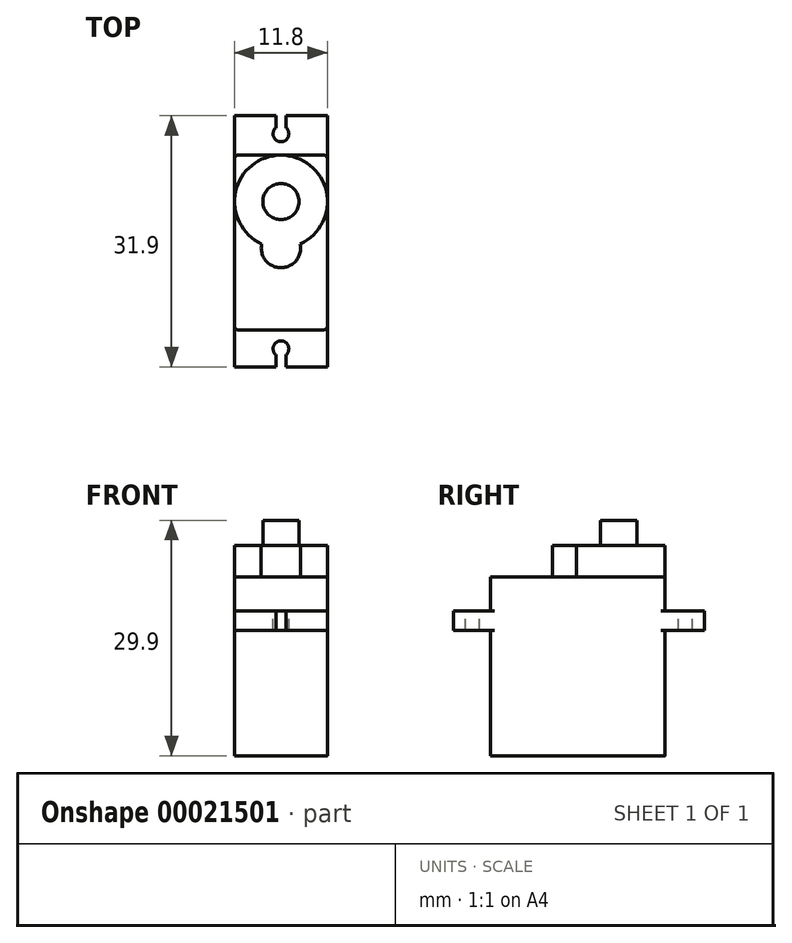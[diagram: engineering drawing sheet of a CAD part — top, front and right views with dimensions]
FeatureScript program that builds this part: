
annotation { "Feature Type Name" : "Feature", "Feature Type Description" : "" }
export const myFeature = defineFeature(function(context is Context, id is Id, definition is map)
    precondition{}
    {
        {
            var Q0;
            Q0=qCreatedBy(makeId("Top.planeOp"),FACE);
            var sketch = newSketch(context, id + "F0", { "sketchPlane" : qUnion([Q0])});
            skLineSegment(sketch, "E0", {"start": v(0, 0.5) * mm, "end": v(0, 21.7) * mm});
            skLineSegment(sketch, "E1", {"start": v(0.5, 22.2) * mm, "end": v(11.3, 22.2) * mm});
            skLineSegment(sketch, "E2", {"start": v(11.8, 21.7) * mm, "end": v(11.8, 0.5) * mm});
            skLineSegment(sketch, "E3", {"start": v(11.3, 0) * mm, "end": v(0.5, 0) * mm});
            skPoint(sketch, "E4.visualSharp", {"position": v(0, 22.2) * mm});
            skArc(sketch, "E4.filletArc", {"start": v(0.5, 22.2) * mm, "mid": v(0.15, 22.05) * mm, "end": v(0, 21.7) * mm});
            skPoint(sketch, "E5.visualSharp", {"position": v(11.8, 22.2) * mm});
            skArc(sketch, "E5.filletArc", {"start": v(11.8, 21.7) * mm, "mid": v(11.65, 22.05) * mm, "end": v(11.3, 22.2) * mm});
            skPoint(sketch, "E6.visualSharp", {"position": v(11.8, 0) * mm});
            skArc(sketch, "E6.filletArc", {"start": v(11.3, 0) * mm, "mid": v(11.65, 0.15) * mm, "end": v(11.8, 0.5) * mm});
            skPoint(sketch, "E7.visualSharp", {"position": v(0, 0) * mm});
            skArc(sketch, "E7.filletArc", {"start": v(0, 0.5) * mm, "mid": v(0.15, 0.15) * mm, "end": v(0.5, 0) * mm});
            skSolve(sketch);
        }
        {
            var Q0;
            Q0=makeQuery(id+"F0.imprint","IMPRINT",FACE,{"disambiguationData":[TD([[makeQuery(id+"F0.imprint","IMPRINT",EDGE,{"derivedFrom":sQuery(id+"F0.wireOp",EDGE,"E0")}),-1.0]])]});
            extrude(context, id + "F1", {"entities" : qUnion([Q0]), "depth" : 16 * mm});
        }
        {
            var Q0;
            Q0=makeQuery(id+"F1.opExtrude","CAP_FACE",FACE,{"disambiguationData":[OSD([sQuery(id+"F0.wireOp",EDGE,"E0"),sQuery(id+"F0.wireOp",EDGE,"E1"),sQuery(id+"F0.wireOp",EDGE,"E2"),sQuery(id+"F0.wireOp",EDGE,"E3"),sQuery(id+"F0.wireOp",EDGE,"E4.filletArc"),sQuery(id+"F0.wireOp",EDGE,"E5.filletArc"),sQuery(id+"F0.wireOp",EDGE,"E6.filletArc"),sQuery(id+"F0.wireOp",EDGE,"E7.filletArc")])],"isStart":false});
            extrude(context, id + "F2", {"entities" : qUnion([Q0]), "operationType" : NewBodyOperationType.ADD, "depth" : 6.7 * mm});
        }
        {
            var Q0;
            Q0=makeQuery(id+"F2.opExtrude","CAP_FACE",FACE,{"disambiguationData":[OSD([sQuery(id+"F0.wireOp",EDGE,"E0"),sQuery(id+"F0.wireOp",EDGE,"E1"),sQuery(id+"F0.wireOp",EDGE,"E2"),sQuery(id+"F0.wireOp",EDGE,"E3"),sQuery(id+"F0.wireOp",EDGE,"E4.filletArc"),sQuery(id+"F0.wireOp",EDGE,"E5.filletArc"),sQuery(id+"F0.wireOp",EDGE,"E6.filletArc"),sQuery(id+"F0.wireOp",EDGE,"E7.filletArc")])],"isStart":false});
            var sketch = newSketch(context, id + "F3", { "sketchPlane" : qUnion([Q0])});
            skLineSegment(sketch, "E8", {"start": v(0, 16.3) * mm, "end": v(11.8, 16.3) * mm, "construction": true});
            skArc(sketch, "E9", {"start": v(8.34, 10.93) * mm, "mid": v(5.9, 22.2) * mm, "end": v(3.46, 10.93) * mm});
            skLineSegment(sketch, "E10", {"start": v(5.9, 16.3) * mm, "end": v(5.9, 5.27) * mm, "construction": true});
            skArc(sketch, "E11", {"start": v(3.46, 10.93) * mm, "mid": v(5.9, 7.9) * mm, "end": v(8.34, 10.93) * mm});
            skSolve(sketch);
        }
        {
            var Q0;
            {var subQ0=sQuery(id+"F3.wireOp",EDGE,"E11");Q0=makeQuery(id+"F3.imprint","IMPRINT",FACE,{"disambiguationData":[TD([[makeQuery(id+"F3.imprint","IMPRINT",EDGE,{"derivedFrom":subQ0}),1.0]])]});}
            extrude(context, id + "F4", {"entities" : qUnion([Q0]), "operationType" : NewBodyOperationType.ADD, "depth" : 4 * mm});
        }
        {
            var Q0;
            Q0=makeQuery(id+"F4.opExtrude","CAP_FACE",FACE,{"disambiguationData":[OSD([sQuery(id+"F3.wireOp",EDGE,"E9"),sQuery(id+"F3.wireOp",EDGE,"E11")])],"isStart":false});
            var sketch = newSketch(context, id + "F5", { "sketchPlane" : qUnion([Q0])});
            skLineSegment(sketch, "E12", {"start": v(5.9, 22.2) * mm, "end": v(5.9, 7.9) * mm, "construction": true});
            skLineSegment(sketch, "E13", {"start": v(0, 16.3) * mm, "end": v(11.8, 16.3) * mm, "construction": true});
            skCircle(sketch, "E14", {"center": v(5.9, 16.3) * mm, "radius": 2.3 * mm});
            skSolve(sketch);
        }
        {
            var Q0;
            Q0=makeQuery(id+"F5.imprint","IMPRINT",FACE,{"disambiguationData":[TD([[makeQuery(id+"F5.imprint","IMPRINT",EDGE,{"derivedFrom":sQuery(id+"F5.wireOp",EDGE,"E14")}),1.0]])]});
            extrude(context, id + "F6", {"entities" : qUnion([Q0]), "operationType" : NewBodyOperationType.ADD, "depth" : 3.2 * mm});
        }
        {
            var Q0;
            {var subQ0=sQuery(id+"F0.wireOp",EDGE,"E3");Q0=makeQuery(id+"F2.boolean.opBoolean","MERGE",FACE,{"derivedFrom":[makeQuery(id+"F1.opExtrude","SWEPT_FACE",FACE,{"disambiguationData":[OSD([subQ0])]}),makeQuery(id+"F2.opExtrude","SWEPT_FACE",FACE,{"disambiguationData":[OSD([subQ0])]})]});}
            var sketch = newSketch(context, id + "F7", { "sketchPlane" : qUnion([Q0])});
            skLineSegment(sketch, "E15", {"start": v(5.9, 22.7) * mm, "end": v(5.9, 0) * mm, "construction": true});
            skLineSegment(sketch, "E16", {"start": v(0.5, 18.4) * mm, "end": v(11.3, 18.4) * mm, "construction": true});
            skLineSegment(sketch, "E17", {"start": v(0, 18.4) * mm, "end": v(11.8, 18.4) * mm});
            skLineSegment(sketch, "E18", {"start": v(11.8, 18.4) * mm, "end": v(11.8, 15.9) * mm});
            skLineSegment(sketch, "E19", {"start": v(11.8, 15.9) * mm, "end": v(0, 15.9) * mm});
            skLineSegment(sketch, "E20", {"start": v(0, 15.9) * mm, "end": v(0, 18.4) * mm});
            skSolve(sketch);
        }
        {
            var Q0;
            {var subQ7=sQuery(id+"F7.wireOp",EDGE,"E18");Q0=makeQuery(id+"F7.imprint","IMPRINT",FACE,{"disambiguationData":[TD([[makeQuery(id+"F7.imprint","IMPRINT",EDGE,{"derivedFrom":subQ7}),-1.0]])]});}
            var Q1;
            {var subQ0=sQuery(id+"F0.wireOp",EDGE,"E3");var subQ1=sQuery(id+"F0.wireOp",EDGE,"E7.filletArc");var subQ2=makeQuery(id+"F2.boolean.opBoolean","MERGE",EDGE,{"derivedFrom":[makeQuery(id+"F1.opExtrude","SWEPT_EDGE",EDGE,{"disambiguationData":[OSD([subQ0,subQ1])]}),makeQuery(id+"F2.opExtrude","SWEPT_EDGE",EDGE,{"disambiguationData":[OSD([subQ0,subQ1])]})]});var subQ5=sQuery(id+"F7.wireOp",EDGE,"E17");var subQ6=makeQuery(id+"F7.imprint","INTERSECT",VERTEX,{"derivedFrom":[subQ2,subQ5]});Q1=makeQuery(id+"F7.imprint","IMPRINT",FACE,{"disambiguationData":[TD([[makeQuery(id+"F7.imprint","IMPRINT",EDGE,{"disambiguationData":[TD([[subQ6,-1.0]])],"derivedFrom":subQ5}),-1.0]])]});}
            var Q2;
            {var subQ7=sQuery(id+"F7.wireOp",EDGE,"E20");Q2=makeQuery(id+"F7.imprint","IMPRINT",FACE,{"disambiguationData":[TD([[makeQuery(id+"F7.imprint","IMPRINT",EDGE,{"derivedFrom":subQ7}),-1.0]])]});}
            extrude(context, id + "F8", {"entities" : qUnion([Q0, Q1, Q2]), "operationType" : NewBodyOperationType.ADD, "oppositeDirection" : true, "depth" : 1 * mm});
        }
        {
            var Q0;
            {var subQ0=sQuery(id+"F0.wireOp",EDGE,"E3");Q0=makeQuery(id+"F8.boolean.opBoolean","MERGE",FACE,{"derivedFrom":[makeQuery(id+"F2.boolean.opBoolean","MERGE",FACE,{"derivedFrom":[makeQuery(id+"F1.opExtrude","SWEPT_FACE",FACE,{"disambiguationData":[OSD([subQ0])]}),makeQuery(id+"F2.opExtrude","SWEPT_FACE",FACE,{"disambiguationData":[OSD([subQ0])]})]}),makeQuery(id+"F8.opExtrude","CAP_FACE",FACE,{"disambiguationData":[OSD([sQuery(id+"F7.wireOp",EDGE,"E17"),sQuery(id+"F7.wireOp",EDGE,"E18"),sQuery(id+"F7.wireOp",EDGE,"E19"),sQuery(id+"F7.wireOp",EDGE,"E20")])],"isStart":true})]});}
            var sketch = newSketch(context, id + "F9", { "sketchPlane" : qUnion([Q0])});
            skLineSegment(sketch, "E21", {"start": v(0.5, 18.4) * mm, "end": v(11.3, 18.4) * mm});
            skLineSegment(sketch, "E22", {"start": v(0.5, 15.9) * mm, "end": v(11.3, 15.9) * mm});
            skSolve(sketch);
        }
        {
            var Q0;
            Q0=makeQuery(id+"F9.imprint","IMPRINT",FACE,{"disambiguationData":[TD([[makeQuery(id+"F9.imprint","IMPRINT",EDGE,{"derivedFrom":sQuery(id+"F9.wireOp",EDGE,"E21")}),-1.0]])]});
            extrude(context, id + "F10", {"entities" : qUnion([Q0]), "operationType" : NewBodyOperationType.ADD, "depth" : 4.7 * mm});
        }
        {
            var Q0;
            Q0=makeQuery(id+"F10.opExtrude","CAP_FACE",FACE,{"disambiguationData":[OSD([sQuery(id+"F7.wireOp",EDGE,"E17"),sQuery(id+"F7.wireOp",EDGE,"E18"),sQuery(id+"F7.wireOp",EDGE,"E19"),sQuery(id+"F7.wireOp",EDGE,"E20"),sQuery(id+"F9.wireOp",EDGE,"E21"),sQuery(id+"F9.wireOp",EDGE,"E22")])],"isStart":false});
            extrude(context, id + "F11", {"entities" : qUnion([Q0]), "operationType" : NewBodyOperationType.ADD, "oppositeDirection" : true, "depth" : 31.9 * mm});
        }
        {
            var Q0;
            {var subQ0=sQuery(id+"F7.wireOp",EDGE,"E17");var subQ1=makeQuery(id+"F8.opExtrude","SWEPT_FACE",FACE,{"disambiguationData":[OSD([subQ0])]});var subQ8=sQuery(id+"F0.wireOp",EDGE,"E0");var subQ10=sQuery(id+"F0.wireOp",EDGE,"E2");Q0=makeQuery(id+"F10.boolean.opBoolean","MERGE",FACE,{"derivedFrom":[makeQuery(id+"F8.boolean.opBoolean","SPLIT",FACE,{"disambiguationData":[TD([makeQuery(id+"F1.opExtrude","SWEPT_FACE",FACE,{"disambiguationData":[OSD([subQ8])]})])],"derivedFrom":subQ1}),makeQuery(id+"F8.boolean.opBoolean","SPLIT",FACE,{"disambiguationData":[TD([makeQuery(id+"F1.opExtrude","SWEPT_FACE",FACE,{"disambiguationData":[OSD([subQ10])]})])],"derivedFrom":subQ1}),makeQuery(id+"F10.opExtrude","SWEPT_FACE",FACE,{"disambiguationData":[OSD([subQ0,sQuery(id+"F9.wireOp",EDGE,"E21")])]})]});}
            var sketch = newSketch(context, id + "F12", { "sketchPlane" : qUnion([Q0])});
            skLineSegment(sketch, "E23", {"start": v(0, -2.4) * mm, "end": v(11.8, -2.4) * mm, "construction": true});
            skArc(sketch, "E24", {"start": v(6.55, -3.16) * mm, "mid": v(5.9, -1.4) * mm, "end": v(5.25, -3.16) * mm});
            skLineSegment(sketch, "E25", {"start": v(5.9, -2.4) * mm, "end": v(5.9, -4.7) * mm, "construction": true});
            skLineSegment(sketch, "E26", {"start": v(6.55, -4.7) * mm, "end": v(6.55, -3.16) * mm});
            skLineSegment(sketch, "E27", {"start": v(5.25, -4.7) * mm, "end": v(5.25, -3.16) * mm});
            skSolve(sketch);
        }
        {
            var Q0;
            Q0=makeQuery(id+"F12.imprint","IMPRINT",FACE,{"disambiguationData":[TD([[makeQuery(id+"F12.imprint","IMPRINT",EDGE,{"derivedFrom":sQuery(id+"F12.wireOp",EDGE,"E24")}),1.0]])]});
            extrude(context, id + "F13", {"entities" : qUnion([Q0]), "operationType" : NewBodyOperationType.REMOVE, "endBound" : BoundingType.UP_TO_NEXT, "oppositeDirection" : true, "depth" : 25.4 * mm});
        }
        {
            var Q0;
            Q0=makeQuery(id+"F11.opExtrude","SWEPT_FACE",FACE,{"disambiguationData":[OSD([sQuery(id+"F7.wireOp",EDGE,"E17"),sQuery(id+"F9.wireOp",EDGE,"E21")])]});
            var sketch = newSketch(context, id + "F14", { "sketchPlane" : qUnion([Q0])});
            skLineSegment(sketch, "E28", {"start": v(0, 24.9) * mm, "end": v(11.8, 24.9) * mm, "construction": true});
            skArc(sketch, "E29", {"start": v(5.25, 25.66) * mm, "mid": v(5.9, 23.9) * mm, "end": v(6.55, 25.66) * mm});
            skLineSegment(sketch, "E30", {"start": v(5.9, 24.9) * mm, "end": v(5.9, 27.2) * mm, "construction": true});
            skLineSegment(sketch, "E31", {"start": v(5.25, 27.2) * mm, "end": v(5.25, 25.66) * mm});
            skLineSegment(sketch, "E32", {"start": v(6.55, 27.2) * mm, "end": v(6.55, 25.66) * mm});
            skSolve(sketch);
        }
        {
            var Q0;
            Q0=makeQuery(id+"F14.imprint","IMPRINT",FACE,{"disambiguationData":[TD([[makeQuery(id+"F14.imprint","IMPRINT",EDGE,{"derivedFrom":sQuery(id+"F14.wireOp",EDGE,"E29")}),1.0]])]});
            extrude(context, id + "F15", {"entities" : qUnion([Q0]), "operationType" : NewBodyOperationType.REMOVE, "endBound" : BoundingType.UP_TO_NEXT, "oppositeDirection" : true, "depth" : 25.4 * mm});
        }
    });
